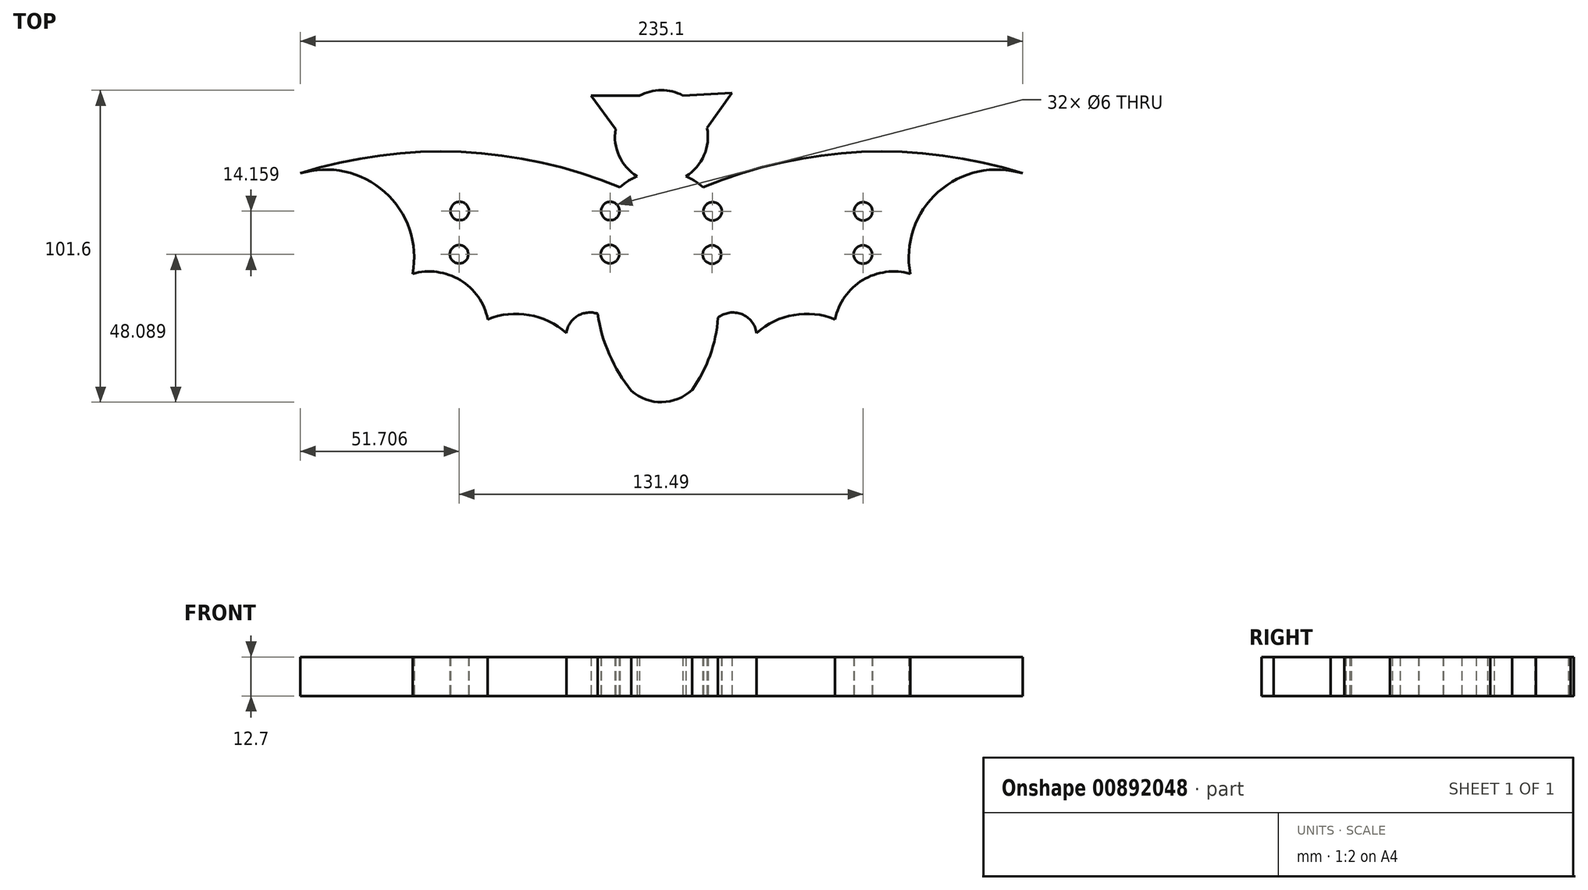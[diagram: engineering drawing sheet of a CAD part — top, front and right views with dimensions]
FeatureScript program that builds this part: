
annotation { "Feature Type Name" : "Feature", "Feature Type Description" : "" }
export const myFeature = defineFeature(function(context is Context, id is Id, definition is map)
    precondition{}
    {
        {
            var Q0;
            Q0=qCreatedBy(makeId("Top.planeOp"),FACE);
            var sketch = newSketch(context, id + "F0", { "sketchPlane" : qUnion([Q0])});
            skArc(sketch, "E0", {"start": v(7.94, 18.42) * mm, "mid": v(13.85, 25.2) * mm, "end": v(14.87, 34.15) * mm});
            skLineSegment(sketch, "E1", {"start": v(-7.15, 44.65) * mm, "end": v(-22.94, 44.65) * mm});
            skLineSegment(sketch, "E2", {"start": v(-22.94, 44.65) * mm, "end": v(-14.94, 33.77) * mm});
            skLineSegment(sketch, "E3", {"start": v(7, 44.73) * mm, "end": v(22.91, 45.52) * mm});
            skLineSegment(sketch, "E4", {"start": v(22.91, 45.52) * mm, "end": v(14.87, 34.15) * mm});
            skArc(sketch, "E5", {"start": v(13.55, 14.79) * mm, "mid": v(10.9, 16.84) * mm, "end": v(7.94, 18.42) * mm});
            skArc(sketch, "E6", {"start": v(-9.77, -51.46) * mm, "mid": v(0.13, -55.16) * mm, "end": v(9.92, -51.17) * mm});
            skArc(sketch, "E7", {"start": v(-20.76, -26.36) * mm, "mid": v(-16.95, -39.65) * mm, "end": v(-9.77, -51.46) * mm});
            skArc(sketch, "E8", {"start": v(9.92, -51.17) * mm, "mid": v(15.8, -40.01) * mm, "end": v(18.39, -27.66) * mm});
            skArc(sketch, "E9.trimOffspring", {"start": v(-7.94, 18.42) * mm, "mid": v(-12.85, 15.4) * mm, "end": v(-16.7, 11.1) * mm});
            skArc(sketch, "E10.trimOffspring", {"start": v(-14.94, 33.77) * mm, "mid": v(-13.77, 25.03) * mm, "end": v(-7.94, 18.42) * mm});
            skArc(sketch, "E11.trimOffspring", {"start": v(7, 44.73) * mm, "mid": v(-0.08, 46.44) * mm, "end": v(-7.15, 44.65) * mm});
            skArc(sketch, "E12", {"start": v(117.55, 19.36) * mm, "mid": v(65.14, 26.33) * mm, "end": v(13.55, 14.79) * mm});
            skArc(sketch, "E13", {"start": v(117.55, 19.36) * mm, "mid": v(90.05, 13.3) * mm, "end": v(80.98, -13.37) * mm});
            skArc(sketch, "E14", {"start": v(80.98, -13.37) * mm, "mid": v(65.5, -15.4) * mm, "end": v(56.5, -28.17) * mm});
            skArc(sketch, "E15", {"start": v(56.5, -28.17) * mm, "mid": v(43.1, -26.77) * mm, "end": v(30.93, -32.61) * mm});
            skArc(sketch, "E16", {"start": v(30.93, -32.61) * mm, "mid": v(26.1, -26.5) * mm, "end": v(18.39, -27.66) * mm});
            skArc(sketch, "E17.MirrorCS", {"start": v(-117.55, 19.36) * mm, "mid": v(-65.14, 26.33) * mm, "end": v(-13.55, 14.79) * mm});
            skArc(sketch, "E18.MirrorCS", {"start": v(-117.55, 19.36) * mm, "mid": v(-90.05, 13.3) * mm, "end": v(-80.98, -13.37) * mm});
            skArc(sketch, "E19.MirrorCS", {"start": v(-80.98, -13.37) * mm, "mid": v(-65.5, -15.4) * mm, "end": v(-56.5, -28.17) * mm});
            skArc(sketch, "E20.MirrorCS", {"start": v(-56.5, -28.17) * mm, "mid": v(-43.1, -26.77) * mm, "end": v(-30.93, -32.61) * mm});
            skArc(sketch, "E21.MirrorCS", {"start": v(-30.93, -32.61) * mm, "mid": v(-27.31, -27.1) * mm, "end": v(-20.76, -26.36) * mm});
            skArc(sketch, "E22", {"start": v(99.6, -43.85) * mm, "mid": v(99.87, -43.5) * mm, "end": v(100.13, -43.15) * mm});
            skCircle(sketch, "E23", {"center": v(16.45, -7.07) * mm, "radius": 3 * mm});
            skCircle(sketch, "E24.7.0.0", {"center": v(16.65, 7) * mm, "radius": 3 * mm});
            skCircle(sketch, "E24.14.0.0", {"center": v(65.65, 7) * mm, "radius": 3 * mm});
            skCircle(sketch, "E25.4.0.0", {"center": v(65.56, -7.05) * mm, "radius": 3 * mm});
            skArc(sketch, "E26", {"start": v(101.23, 42.76) * mm, "mid": v(101.2, 42.84) * mm, "end": v(101.2, 42.92) * mm});
            skCircle(sketch, "E27", {"center": v(-65.84, -6.98) * mm, "radius": 3 * mm});
            skCircle(sketch, "E28.7.0.0", {"center": v(-65.65, 7.09) * mm, "radius": 3 * mm});
            skCircle(sketch, "E28.14.0.0", {"center": v(-16.65, 7.09) * mm, "radius": 3 * mm});
            skCircle(sketch, "E29.4.0.0", {"center": v(-16.74, -6.96) * mm, "radius": 3 * mm});
            skPoint(sketch, "E30.orphan", {"position": v(-18.39, -27.66) * mm});
            skSolve(sketch);
        }
        {
            var Q0;
            Q0=makeQuery(id+"F0.imprint","IMPRINT",FACE,{"disambiguationData":[TD([[makeQuery(id+"F0.imprint","IMPRINT",EDGE,{"derivedFrom":sQuery(id+"F0.wireOp",EDGE,"E0")}),1.0]])]});
            extrude(context, id + "F1", {"entities" : qUnion([Q0]), "depth" : 12.7 * mm, "offsetDistance" : 25.4 * mm});
        }
    });
